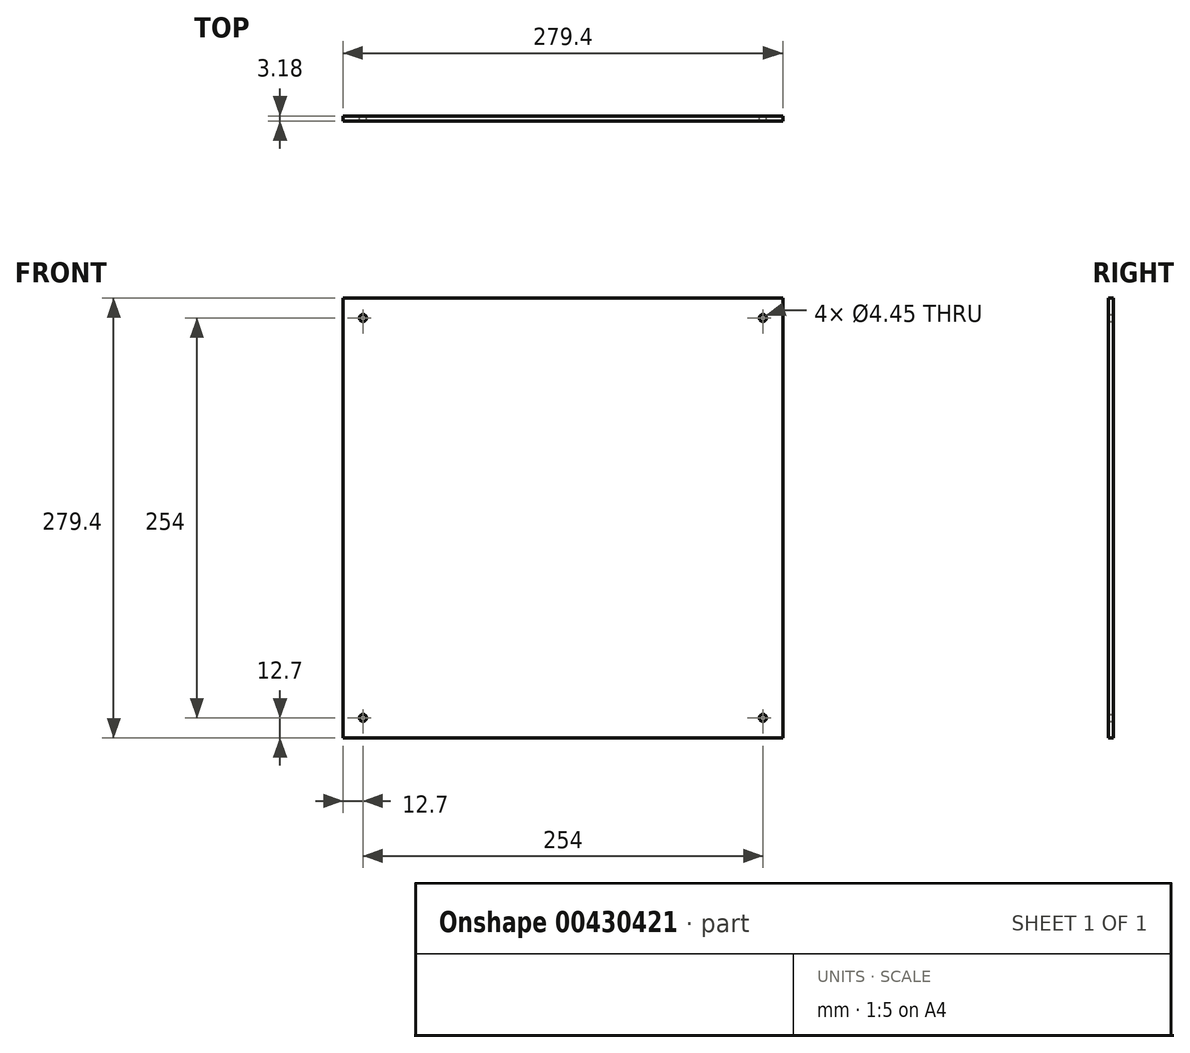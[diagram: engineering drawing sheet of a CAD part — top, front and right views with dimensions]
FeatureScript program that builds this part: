
annotation { "Feature Type Name" : "Feature", "Feature Type Description" : "" }
export const myFeature = defineFeature(function(context is Context, id is Id, definition is map)
    precondition{}
    {
        {
            var Q0;
            Q0=qCreatedBy(makeId("Front.planeOp"),FACE);
            var sketch = newSketch(context, id + "F0", { "sketchPlane" : qUnion([Q0])});
            skLineSegment(sketch, "E0.bottom", {"start": v(-139.7, 139.7) * mm, "end": v(139.7, 139.7) * mm});
            skLineSegment(sketch, "E0.top", {"start": v(-139.7, -139.7) * mm, "end": v(139.7, -139.7) * mm});
            skLineSegment(sketch, "E0.left", {"start": v(-139.7, 139.7) * mm, "end": v(-139.7, -139.7) * mm});
            skLineSegment(sketch, "E0.right", {"start": v(139.7, 139.7) * mm, "end": v(139.7, -139.7) * mm});
            skPoint(sketch, "E0.middle", {"position": v(0, 0) * mm});
            skLineSegment(sketch, "E1.bottom", {"start": v(-127, 127) * mm, "end": v(127, 127) * mm, "construction": true});
            skLineSegment(sketch, "E1.top", {"start": v(-127, -127) * mm, "end": v(127, -127) * mm, "construction": true});
            skLineSegment(sketch, "E1.left", {"start": v(-127, 127) * mm, "end": v(-127, -127) * mm, "construction": true});
            skLineSegment(sketch, "E1.right", {"start": v(127, 127) * mm, "end": v(127, -127) * mm, "construction": true});
            skCircle(sketch, "E2", {"center": v(-127, -127) * mm, "radius": 2.22 * mm});
            skCircle(sketch, "E3", {"center": v(-127, 127) * mm, "radius": 2.22 * mm});
            skCircle(sketch, "E4", {"center": v(127, 127) * mm, "radius": 2.22 * mm});
            skCircle(sketch, "E5", {"center": v(127, -127) * mm, "radius": 2.22 * mm});
            skSolve(sketch);
        }
        {
            var Q0;
            Q0 = qSketchRegion(id + "F0", true);
            extrude(context, id + "F1", {"entities" : qUnion([Q0]), "depth" : 3.17 * mm, "offsetDistance" : 25.4 * mm});
        }
    });
